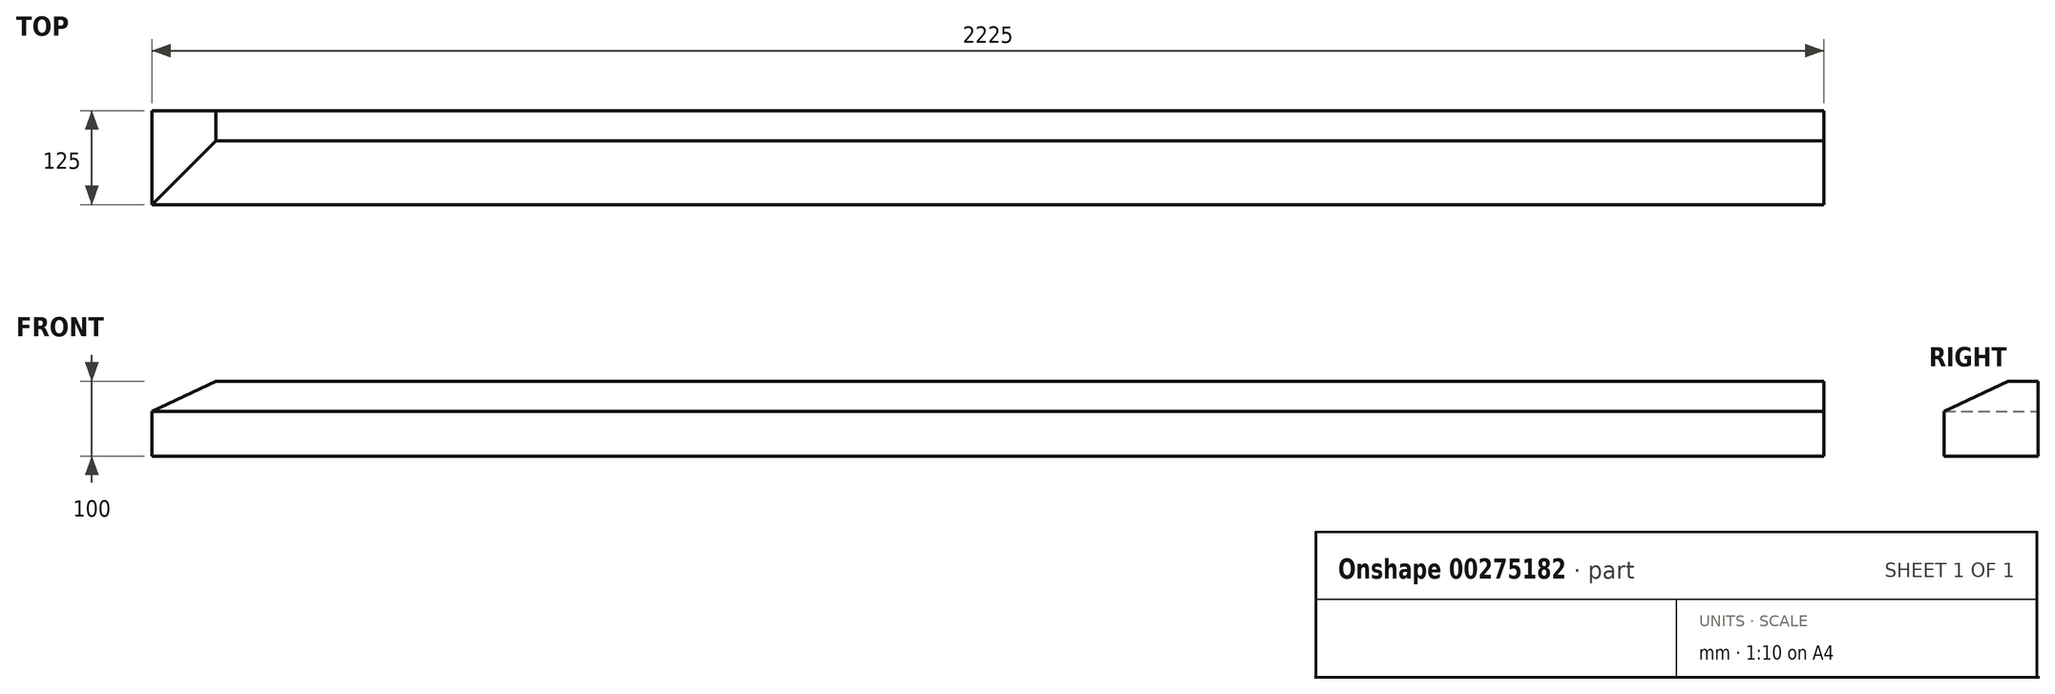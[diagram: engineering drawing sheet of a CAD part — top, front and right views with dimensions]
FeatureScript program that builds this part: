
annotation { "Feature Type Name" : "Feature", "Feature Type Description" : "" }
export const myFeature = defineFeature(function(context is Context, id is Id, definition is map)
    precondition{}
    {
        {
            var Q0;
            Q0=qCreatedBy(makeId("Front.planeOp"),FACE);
            var sketch = newSketch(context, id + "F0", { "sketchPlane" : qUnion([Q0])});
            skLineSegment(sketch, "E0.bottom", {"start": v(0, 0) * mm, "end": v(-2225, 0) * mm});
            skLineSegment(sketch, "E0.top", {"start": v(0, -100) * mm, "end": v(-2225, -100) * mm});
            skLineSegment(sketch, "E0.left", {"start": v(0, 0) * mm, "end": v(0, -100) * mm});
            skLineSegment(sketch, "E0.right", {"start": v(-2225, 0) * mm, "end": v(-2225, -100) * mm});
            skSolve(sketch);
        }
        {
            var Q0;
            Q0=makeQuery(id+"F0.imprint","IMPRINT",FACE,{"disambiguationData":[TD([[makeQuery(id+"F0.imprint","IMPRINT",EDGE,{"derivedFrom":sQuery(id+"F0.wireOp",EDGE,"E0.bottom")}),1.0]])]});
            extrude(context, id + "F1", {"entities" : qUnion([Q0]), "depth" : 125 * mm});
        }
        {
            var Q0;
            Q0=makeQuery(id+"F1.opExtrude","CAP_EDGE",EDGE,{"disambiguationData":[OSD([sQuery(id+"F0.wireOp",EDGE,"E0.bottom")])],"isStart":false});
            var Q1;
            Q1=makeQuery(id+"F1.opExtrude","SWEPT_EDGE",EDGE,{"disambiguationData":[OSD([sQuery(id+"F0.wireOp",EDGE,"E0.bottom"),sQuery(id+"F0.wireOp",EDGE,"E0.right")])]});
            chamfer(context, id + "F2", {"entities" : qUnion([Q0, Q1]), "chamferType" : ChamferType.TWO_OFFSETS, "width1" : 40 * mm, "oppositeDirection" : false, "width2" : 85 * mm, "tangentPropagation" : true});
        }
    });
